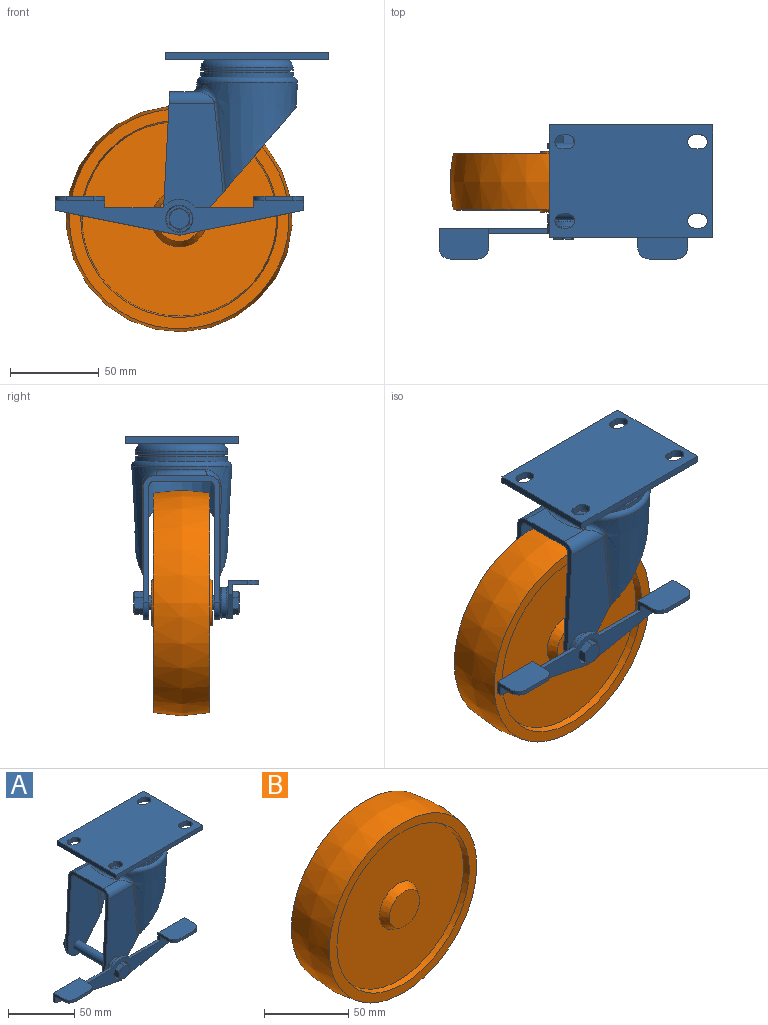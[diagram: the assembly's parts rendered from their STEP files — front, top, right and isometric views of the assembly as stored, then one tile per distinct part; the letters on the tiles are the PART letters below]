
ASSEMBLY  parts=2 mates=1
PART A: 114 faces, bbox 154.5x75.8x104.2 mm
  f0: torus R=31.36mm, axis (0,0,-1), area 285mm2, adj f7,f55,f56,f61
  f1: torus R=31.36mm, axis (0,0,-1), area 153.3mm2, adj f11,f45,f50,f51
  f2: torus R=9.92mm, axis (0,-1,0), area 70.3mm2, adj f4,f89,f94,f96
  f3: torus R=7.64mm, axis (0,1,0), area 78.3mm2, adj f4,f16
  f4: cone r=8.57mm half-angle=5deg, axis (0,-1,0), area 167.4mm2, adj f2,f3,f94,f95,f96
  f5: cone r=7.72mm half-angle=5deg, axis (0,-1,0), area 196.3mm2, adj f75,f76
  f6: cylinder r=3.97mm len=36.83mm, axis (0,1,0), area 918.4mm2, adj f43,f44
  f7: cone r=25.28mm half-angle=3deg, axis (0,0,1), area 3819.6mm2, adj f0,f53,f54,f55,f56,f57,f58
  f8: cylinder r=9.13mm len=16.08mm, axis (0,1,0), area 72.1mm2, adj f16,f44,f52,f53
  f9: cylinder r=9.13mm len=16.08mm, axis (0,1,0), area 72.1mm2, adj f42,f43,f52,f53
  f10: torus R=25.1mm, axis (0,0,-1), area 879.5mm2, adj f11,f17
  f11: cone r=28.45mm half-angle=3deg, axis (0,0,1), area 4113.4mm2, adj f1,f10,f48,f49,f50,f51,f53
  f12: cylinder r=25.91mm len=51.82mm, axis (0,0,1), area 413.5mm2, adj f17,f41
  f13: cylinder r=24.13mm len=48.26mm, axis (0,0,1), area 173.3mm2, adj f40,f41
  f14: cylinder r=25.91mm len=51.82mm, axis (0,0,1), area 248.1mm2, adj f15,f40
  f15: torus R=21.15mm, axis (0,0,1), area 1136.4mm2, adj f14,f18
  f16: plane 74.22x33.7mm, normal (0,-1,0), area 1817.1mm2, adj f3,f8,f46,f49,f52,f53
  f17: plane 51.82x51.82mm, normal (0,0,-1), area 129.1mm2, adj f10,f12
  f18: plane 92.08x63.5mm, normal (0,0,-1), area 4143.3mm2, adj f15,f19,f20,f21,f22,f24,f25,f26
  f19: plane 63.5x3.96mm, normal (-1,0,0), area 251.6mm2, adj f18,f20,f22,f23
  f20: plane 92.08x3.96mm, normal (0,1,0), area 364.8mm2, adj f18,f19,f21,f23
  f21: plane 63.5x3.96mm, normal (1,0,0), area 251.6mm2, adj f18,f20,f22,f23
  f22: plane 92.08x3.96mm, normal (0,-1,0), area 364.8mm2, adj f18,f19,f21,f23
  f23: plane 92.08x63.5mm, normal (0,0,1), area 5548mm2, adj f19,f20,f21,f22,f24,f25,f26,f27
  f24: cylinder r=3.97mm len=7.94mm, axis (0,0,1), area 49.4mm2, adj f18,f23,f25,f27
  f25: plane 3.96x3.18mm, normal (0,-1,0), area 12.6mm2, adj f18,f23,f24,f26
  f26: cylinder r=3.97mm len=7.94mm, axis (0,0,1), area 49.4mm2, adj f18,f23,f25,f27
  f27: plane 3.96x3.18mm, normal (0,1,0), area 12.6mm2, adj f18,f23,f24,f26
  f28: cylinder r=3.97mm len=7.94mm, axis (0,0,1), area 49.4mm2, adj f18,f23,f29,f31
  f29: plane 3.96x3.18mm, normal (0,1,0), area 12.6mm2, adj f18,f23,f28,f30
  f30: cylinder r=3.97mm len=7.94mm, axis (0,0,1), area 49.4mm2, adj f18,f23,f29,f31
  f31: plane 3.96x3.18mm, normal (0,-1,0), area 12.6mm2, adj f18,f23,f28,f30
  f32: cylinder r=3.97mm len=7.94mm, axis (0,0,1), area 49.4mm2, adj f18,f23,f33,f35
  f33: plane 3.96x3.18mm, normal (0,1,0), area 12.6mm2, adj f18,f23,f32,f34
  f34: cylinder r=3.97mm len=7.94mm, axis (0,0,1), area 49.4mm2, adj f18,f23,f33,f35
  f35: plane 3.96x3.18mm, normal (0,-1,0), area 12.6mm2, adj f18,f23,f32,f34
  f36: cylinder r=3.97mm len=7.94mm, axis (0,0,1), area 49.4mm2, adj f18,f23,f37,f39
  f37: plane 3.96x3.18mm, normal (0,-1,0), area 12.6mm2, adj f18,f23,f36,f38
  f38: cylinder r=3.97mm len=7.94mm, axis (0,0,1), area 49.4mm2, adj f18,f23,f37,f39
  f39: plane 3.96x3.18mm, normal (0,1,0), area 12.6mm2, adj f18,f23,f36,f38
  f40: plane 51.82x51.82mm, normal (0,0,-1), area 279.5mm2, adj f13,f14
  f41: plane 51.82x51.82mm, normal (0,0,1), area 279.5mm2, adj f12,f13
  f42: plane 74.22x33.7mm, normal (0,1,0), area 1893.6mm2, adj f9,f47,f48,f52,f53,f62,f63,f64
  f43: plane 74.22x33.7mm, normal (0,-1,0), area 1951.1mm2, adj f6,f9,f52,f53,f58,f59
  f44: plane 74.22x33.7mm, normal (0,1,0), area 1951.1mm2, adj f6,f8,f52,f53,f57,f60
  f45: plane 30.48x16.09mm, normal (0,0,1), area 409.1mm2, adj f1,f46,f47,f52
  f46: cylinder r=6.35mm len=25.42mm, axis (1,0,0), area 207mm2, adj f16,f45,f51,f52
  f47: cylinder r=6.35mm len=25.42mm, axis (-1,0,0), area 207mm2, adj f42,f45,f50,f52
  f48: bspline ~50.54x6.4mm, area 91.4mm2, adj f11,f42,f50,f53
  f49: bspline ~50.54x6.4mm, area 91.4mm2, adj f11,f16,f51,f53
  f50: bspline ~10.89x9.69mm, area 51.2mm2, adj f1,f11,f47,f48
  f51: bspline ~10.89x9.69mm, area 51.2mm2, adj f1,f11,f46,f49
  f52: plane 71.19x43.41mm, normal (-1,0,0.05), area 555.3mm2, adj f8,f9,f16,f42,f43,f44,f45,f46
  f53: plane 68.86x58.79mm, normal (0.76,0,-0.65), area 715.7mm2, adj f7,f8,f9,f11,f16,f42,f43,f44
  f54: plane 50.2x50.2mm, normal (0,0,-1), area 1979.6mm2, adj f7
  f55: bspline ~12.78x9.86mm, area 80.2mm2, adj f0,f7,f58,f59
  f56: bspline ~12.78x9.86mm, area 80.2mm2, adj f0,f7,f57,f60
  f57: bspline ~51x7.95mm, area 180.4mm2, adj f7,f44,f53,f56
  f58: bspline ~51x7.95mm, area 180.4mm2, adj f7,f43,f53,f55
  f59: cylinder r=3.17mm len=25.42mm, axis (-1,0,0), area 103.9mm2, adj f43,f52,f55,f61
  f60: cylinder r=3.17mm len=25.42mm, axis (1,0,0), area 103.9mm2, adj f44,f52,f56,f61
  f61: plane 30.48x16.26mm, normal (0,0,-1), area 414.2mm2, adj f0,f52,f59,f60
  f62: plane 6.08x5.68mm, normal (-0.5,0,-0.87), area 32mm2, adj f42,f63,f67,f69,f70
  f63: plane 6.08x5.68mm, normal (0.5,0,-0.87), area 32mm2, adj f42,f62,f64,f68,f69
  f64: plane 6.95x5.69mm, normal (1,0,0), area 32mm2, adj f42,f63,f65,f68,f73
  f65: plane 6.08x5.68mm, normal (0.5,0,0.87), area 32mm2, adj f42,f64,f66,f72,f73
  f66: plane 6.08x5.68mm, normal (-0.5,0,0.87), area 32mm2, adj f42,f65,f67,f71,f72
  f67: plane 6.95x5.69mm, normal (-1,0,0), area 32mm2, adj f42,f62,f66,f70,f71
  f68: cone r=5.56mm half-angle=60deg, axis (0,-1,0), area 3mm2, adj f63,f64,f74
  f69: cone r=5.56mm half-angle=60deg, axis (0,-1,0), area 3mm2, adj f62,f63,f74
  f70: cone r=5.56mm half-angle=60deg, axis (0,-1,0), area 3mm2, adj f62,f67,f74
  f71: cone r=5.56mm half-angle=60deg, axis (0,-1,0), area 3mm2, adj f66,f67,f74
  f72: cone r=5.56mm half-angle=60deg, axis (0,-1,0), area 3mm2, adj f65,f66,f74
  f73: cone r=5.56mm half-angle=60deg, axis (0,-1,0), area 3mm2, adj f64,f65,f74
  f74: plane 11.11x11.11mm, normal (0,1,0), area 97mm2, adj f68,f69,f70,f71,f72,f73
  f75: plane 14.72x14.72mm, normal (0,-1,0), area 63.1mm2, adj f5,f108,f109,f110,f111,f112,f113
  f76: plane 139.7x20mm, normal (0,-1,0), area 1279.1mm2, adj f5,f77,f78,f79,f80,f81,f83,f84
  f77: plane 10.8x7.94mm, normal (-1,0,0), area 41.1mm2, adj f76,f78,f88,f89,f90,f100
  f78: plane 68.16x13.65mm, normal (-0.2,0,-0.98), area 176.4mm2, adj f76,f77,f79,f89,f94
  f79: cylinder r=8.99mm len=3.52mm, axis (0,1,0), area 9mm2, adj f76,f78,f80,f95
  f80: plane 68.15x13.64mm, normal (0.2,0,-0.98), area 176.4mm2, adj f76,f79,f81,f89,f96
  f81: plane 10.8x7.94mm, normal (1,0,0), area 41.1mm2, adj f76,f80,f82,f89,f92,f97
  f82: plane 27.94x17.15mm, normal (0,0,1), area 461.7mm2, adj f81,f83,f89,f93,f97,f98
  f83: plane 10.8x6.35mm, normal (-1,0,0), area 37.1mm2, adj f76,f82,f84,f89,f92,f98
  f84: plane 32.92x2.54mm, normal (0,0,1), area 83.6mm2, adj f76,f83,f85,f89
  f85: cylinder r=11.01mm len=17.98mm, axis (0,1,0), area 53.5mm2, adj f76,f84,f86,f89
  f86: plane 32.92x2.54mm, normal (0,0,1), area 83.6mm2, adj f76,f85,f87,f89
  f87: plane 10.8x6.35mm, normal (1,0,0), area 37.1mm2, adj f76,f86,f88,f89,f90,f99
  f88: plane 27.94x17.15mm, normal (0,0,1), area 461.7mm2, adj f77,f87,f89,f91,f99,f100
  f89: plane 139.7x20.7mm, normal (0,1,0), area 1307.8mm2, adj f2,f77,f78,f80,f81,f82,f83,f84
  f90: plane 27.94x14.61mm, normal (0,0,-1), area 390.8mm2, adj f76,f77,f87,f91,f99,f100
  f91: plane 15.24x2.54mm, normal (0,-1,0), area 38.7mm2, adj f88,f90,f99,f100
  f92: plane 27.94x14.61mm, normal (0,0,-1), area 390.8mm2, adj f76,f81,f83,f93,f97,f98
  f93: plane 15.24x2.54mm, normal (0,-1,0), area 38.7mm2, adj f82,f92,f97,f98
  f94: bspline ~4.11x1.64mm, area 2.9mm2, adj f2,f4,f78,f95
  f95: torus R=10mm, axis (0,-1,0), area 0.2mm2, adj f4,f79,f94,f96
  f96: bspline ~4.11x1.64mm, area 2.9mm2, adj f2,f4,f80,f95
  f97: cylinder r=6.35mm len=6.35mm, axis (0,0,-1), area 25.3mm2, adj f81,f82,f92,f93
  f98: cylinder r=6.35mm len=6.35mm, axis (0,0,1), area 25.3mm2, adj f82,f83,f92,f93
  f99: cylinder r=6.35mm len=6.35mm, axis (0,0,-1), area 25.3mm2, adj f87,f88,f90,f91
  f100: cylinder r=6.35mm len=6.35mm, axis (0,0,1), area 25.3mm2, adj f77,f88,f90,f91
  f101: plane 11.11x11.11mm, normal (0,-1,0), area 97mm2, adj f102,f103,f104,f105,f106,f107
  f102: cone r=5.56mm half-angle=60deg, axis (0,1,0), area 3mm2, adj f101,f112,f113
  f103: cone r=5.56mm half-angle=60deg, axis (0,1,0), area 3mm2, adj f101,f111,f112
  f104: cone r=5.56mm half-angle=60deg, axis (0,1,0), area 3mm2, adj f101,f110,f111
  f105: cone r=5.56mm half-angle=60deg, axis (0,1,0), area 3mm2, adj f101,f109,f110
  f106: cone r=5.56mm half-angle=60deg, axis (0,1,0), area 3mm2, adj f101,f108,f109
  f107: cone r=5.56mm half-angle=60deg, axis (0,1,0), area 3mm2, adj f101,f108,f113
  f108: plane 8.06x6.95mm, normal (-1,0,0), area 47.2mm2, adj f75,f106,f107,f109,f113
  f109: plane 8.06x6.08mm, normal (-0.5,0,0.87), area 47.2mm2, adj f75,f105,f106,f108,f110
  f110: plane 8.06x6.08mm, normal (0.5,0,0.87), area 47.2mm2, adj f75,f104,f105,f109,f111
  f111: plane 8.06x6.95mm, normal (1,0,0), area 47.2mm2, adj f75,f103,f104,f110,f112
  f112: plane 8.06x6.08mm, normal (0.5,0,-0.87), area 47.2mm2, adj f75,f102,f103,f111,f113
  f113: plane 8.06x6.08mm, normal (-0.5,0,-0.87), area 47.2mm2, adj f75,f102,f107,f108,f112
PART B: 11 faces, bbox 127x34.3x127 mm
  f0: cone r=12.7mm half-angle=30deg, axis (0,-1,0), area 539.5mm2, adj f9,f10
  f1: cone r=54.67mm half-angle=10deg, axis (0,1,0), area 1391mm2, adj f8,f9
  f2: revolved ~127x127mm, area 12653.9mm2, adj f7,f8
  f3: cone r=55.37mm half-angle=10deg, axis (0,-1,0), area 1391mm2, adj f6,f7
  f4: cone r=15.72mm half-angle=30deg, axis (0,1,0), area 539.5mm2, adj f5,f6
  f5: plane 25.4x25.4mm, normal (0,-1,0), area 506.7mm2, adj f4
  f6: plane 109.35x109.35mm, normal (0,-1,0), area 8614.3mm2, adj f3,f4
  f7: plane 123.44x123.44mm, normal (0,-1,0), area 2335.9mm2, adj f2,f3
  f8: plane 123.44x123.44mm, normal (0,1,0), area 2335.9mm2, adj f1,f2
  f9: plane 109.35x109.35mm, normal (0,1,0), area 8614.3mm2, adj f0,f1
  f10: plane 25.4x25.4mm, normal (0,1,0), area 506.7mm2, adj f0
PLACE A at identity
PLACE B at identity
MATE revolute B.f0 <-> A.f2  axis (0,1,0) through (-38.1,17.15,-93.66)mm
